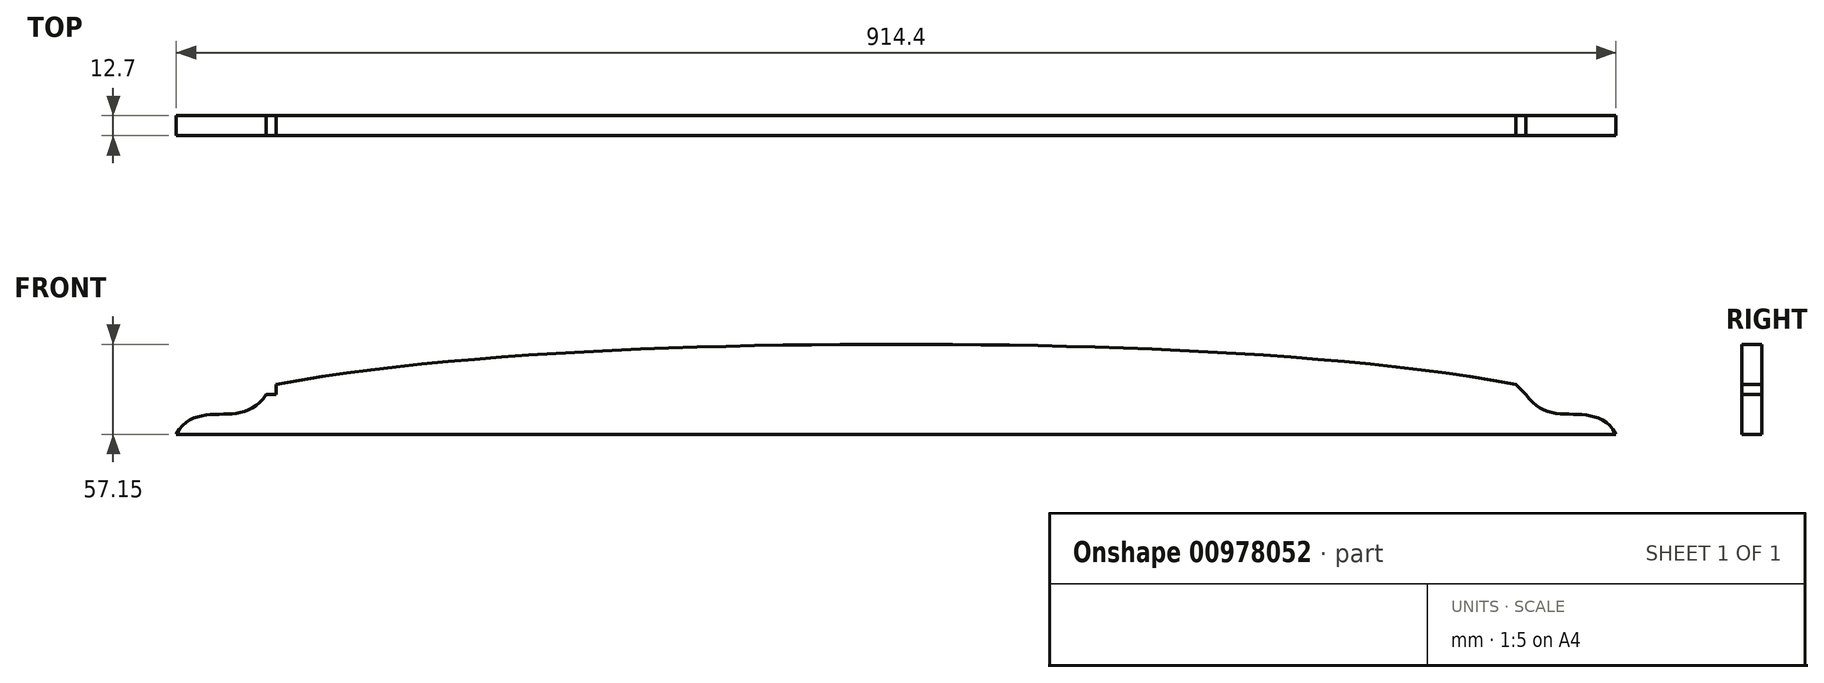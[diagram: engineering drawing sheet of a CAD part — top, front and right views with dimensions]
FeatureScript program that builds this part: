
annotation { "Feature Type Name" : "Feature", "Feature Type Description" : "" }
export const myFeature = defineFeature(function(context is Context, id is Id, definition is map)
    precondition{}
    {
        {
            var Q0;
            Q0=qCreatedBy(makeId("Front.planeOp"),FACE);
            var sketch = newSketch(context, id + "F0", { "sketchPlane" : qUnion([Q0])});
            skLineSegment(sketch, "E0", {"start": v(-457.2, 0) * mm, "end": v(0, 0) * mm});
            skLineSegment(sketch, "E1", {"start": v(0, 0) * mm, "end": v(0, 57.15) * mm, "construction": true});
            skLineSegment(sketch, "E2", {"start": v(-457.2, 0) * mm, "end": v(-400.04, 0) * mm, "construction": true});
            skLineSegment(sketch, "E3", {"start": v(-400.04, 0) * mm, "end": v(-400.04, 25.4) * mm, "construction": true});
            skLineSegment(sketch, "E4", {"start": v(-400.04, 25.4) * mm, "end": v(-457.2, 0) * mm, "construction": true});
            skFitSpline(sketch, "E5", {"points": [v(-393.7, 31.75) * mm, v(0, 57.15) * mm], "startDerivative": vector(326.7, 59.46) * mm, "endDerivative": vector(408.36, 0) * mm});
            skFitSpline(sketch, "E6", {"points": [v(-400.04, 25.4) * mm, v(-428.62, 12.7) * mm, v(-457.2, 0) * mm], "startDerivative": vector(-46.84, -72.23) * mm, "endDerivative": vector(-41.92, -74.55) * mm});
            skFitSpline(sketch, "E7.MirrorCS", {"points": [v(393.7, 31.75) * mm, v(0, 57.15) * mm], "startDerivative": vector(-326.7, 59.46) * mm, "endDerivative": vector(-408.36, 0) * mm});
            skLineSegment(sketch, "E8.MirrorCS", {"start": v(400.04, 25.4) * mm, "end": v(393.7, 31.75) * mm});
            skFitSpline(sketch, "E9.MirrorCS", {"points": [v(400.04, 25.4) * mm, v(428.62, 12.7) * mm, v(457.2, 0) * mm], "startDerivative": vector(46.84, -72.23) * mm, "endDerivative": vector(41.92, -74.55) * mm});
            skLineSegment(sketch, "E10.MirrorCS", {"start": v(457.2, 0) * mm, "end": v(0, 0) * mm});
            skLineSegment(sketch, "E11", {"start": v(-400.04, 25.4) * mm, "end": v(-393.7, 25.4) * mm});
            skLineSegment(sketch, "E12", {"start": v(-393.7, 25.4) * mm, "end": v(-393.7, 31.75) * mm});
            skLineSegment(sketch, "E13.MirrorCS", {"start": v(400.04, 25.4) * mm, "end": v(393.7, 25.4) * mm});
            skLineSegment(sketch, "E14.MirrorCS", {"start": v(393.7, 25.4) * mm, "end": v(393.7, 31.75) * mm});
            skSolve(sketch);
        }
        {
            var Q0;
            Q0 = qSketchRegion(id + "F0", true);
            extrude(context, id + "F1", {"entities" : qUnion([Q0]), "depth" : 12.7 * mm, "offsetDistance" : 25.4 * mm});
        }
    });
